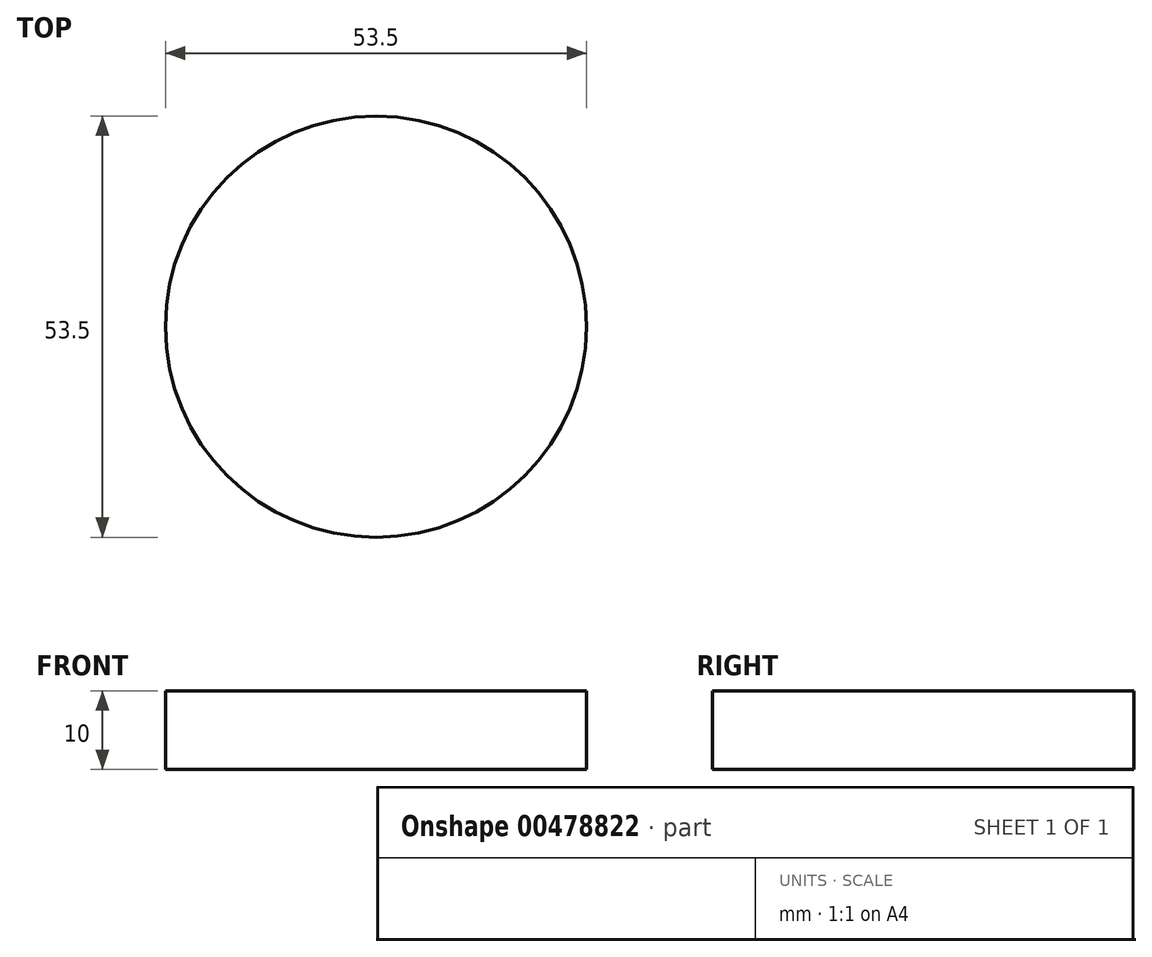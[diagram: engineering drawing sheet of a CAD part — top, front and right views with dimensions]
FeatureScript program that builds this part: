
annotation { "Feature Type Name" : "Feature", "Feature Type Description" : "" }
export const myFeature = defineFeature(function(context is Context, id is Id, definition is map)
    precondition{}
    {
        {
            var Q0;
            Q0=qCreatedBy(makeId("Top.planeOp"),FACE);
            var sketch = newSketch(context, id + "F0", { "sketchPlane" : qUnion([Q0])});
            skCircle(sketch, "E0", {"center": v(0, 0) * mm, "radius": 26.75 * mm});
            skSolve(sketch);
        }
        {
            var Q0;
            Q0=makeQuery(id+"F0.imprint","IMPRINT",FACE,{"disambiguationData":[TD([[makeQuery(id+"F0.imprint","IMPRINT",EDGE,{"derivedFrom":sQuery(id+"F0.wireOp",EDGE,"E0")}),1.0]])]});
            extrude(context, id + "F1", {"entities" : qUnion([Q0]), "depth" : 10 * mm, "offsetDistance" : 25 * mm});
        }
    });
